# Revit family: FA_ШкафГЭШ_EZETEK
name_source: partatom
category: Системы пожарной сигнализации
revit_build: Autodesk Revit 2017 (Build: 20170118_1100(x64)
units: mm (PartAtom-declared; Revit-internal decimal feet)

## family parameters
Всегда вертикально = Да
На основе рабочей плоскости = Нет
Общий = Нет
При загрузке вырезать с полостями = Нет
Размер круглого соединителя = Использовать радиус
Сохранять ориентацию аннотаций = Нет
Тип детали = Нормальный
Точка расчета площади = Нет

## types (2) — shared parameters
ADSK_Версия Revit = 2017
ADSK_Единица измерения = шт.
ADSK_Завод-изготовитель = Ezetek
ADSK_Количество = 1
ADSK_Материал = BIMLIB_Сталь_Нержавеющая_EZETEK
ADSK_Размер_Глубина = 155 мм
URL = https://ezetek.ru
Группа модели = ГЗШ и шкафы ГЗШ
Изготовитель = Ezetek
Описание = Шкафы шины заземления выполнены на основе медной полосы 40х4 мм, помещенной в стальной оцинкованный корпус. Главная заземляющая шина объединяет нулевые защитные и нулевые рабочие совмещенные проводники питающей линии; выводы контура заземления; заземляющие проводники; проводники системы уравнивания потенциалов. Для присоединения проводников используются болты и гайки из нержавеющей стали. Главная заземляющая шина рассчитана на максимальный длительный ток 630 А.

## per-type parameters (varying)
| type | ADSK_Код изделия | ADSK_Марка | ADSK_Масса | ADSK_Масса_Текст | ADSK_Наименование | ADSK_Обозначение | ADSK_Размер_Высота | ADSK_Размер_Ширина |
| Шкаф шины заземления 20 подключений_88042 | 88042 | 88042 | 6.18 | 6.18 | Шкаф шины заземления 20 подключений 600х400х155 мм | 88042 | 600 мм | 400 мм |
| Шкаф шины заземления 10 подключений_88043 | 88043 | 88043 | 3.14 | 3.14 | Шкаф шины заземления 10 подключений 250х300х155 мм | 88043 | 250 мм | 300 мм |
